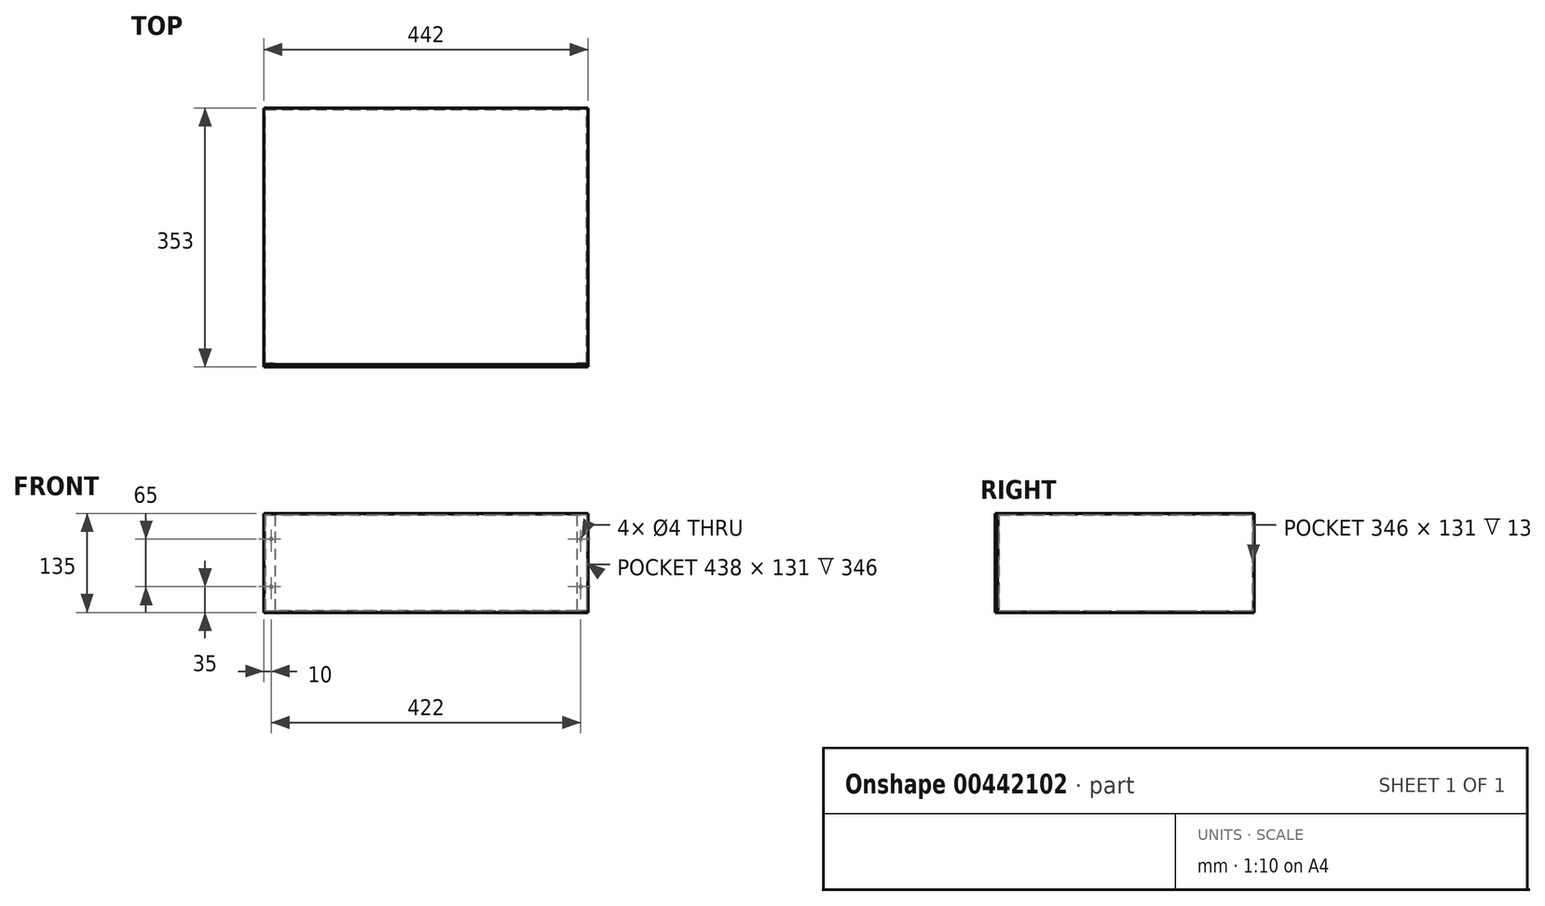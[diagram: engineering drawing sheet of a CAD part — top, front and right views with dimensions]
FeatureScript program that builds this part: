
annotation { "Feature Type Name" : "Feature", "Feature Type Description" : "" }
export const myFeature = defineFeature(function(context is Context, id is Id, definition is map)
    precondition{}
    {
        {
            var Q0;
            Q0=qCreatedBy(makeId("Top.planeOp"),FACE);
            var sketch = newSketch(context, id + "F0", { "sketchPlane" : qUnion([Q0])});
            skLineSegment(sketch, "E0.bottom", {"start": v(221, 175) * mm, "end": v(-221, 175) * mm});
            skLineSegment(sketch, "E0.top", {"start": v(221, -175) * mm, "end": v(-221, -175) * mm});
            skLineSegment(sketch, "E0.left", {"start": v(221, 175) * mm, "end": v(221, -175) * mm});
            skLineSegment(sketch, "E0.right", {"start": v(-221, 175) * mm, "end": v(-221, -175) * mm});
            skPoint(sketch, "E0.middle", {"position": v(0, 0) * mm});
            skSolve(sketch);
        }
        {
            var Q0;
            Q0=qCreatedBy(makeId("Front.planeOp"),FACE);
            cPlane(context, id + "F1", {"entities" : qUnion([Q0]), "cplaneType" : CPlaneType.OFFSET, "offset" : 175 * mm, "width" : 150 * mm, "height" : 150 * mm});
        }
        {
            var Q0;
            Q0=qCreatedBy(makeId("Front.planeOp"),FACE);
            cPlane(context, id + "F2", {"entities" : qUnion([Q0]), "cplaneType" : CPlaneType.OFFSET, "offset" : 175 * mm, "oppositeDirection" : true, "width" : 150 * mm, "height" : 150 * mm});
        }
        {
            var Q0;
            Q0=qCreatedBy(makeId("Top.planeOp"),FACE);
            cPlane(context, id + "F3", {"entities" : qUnion([Q0]), "cplaneType" : CPlaneType.OFFSET, "offset" : 133 * mm, "width" : 150 * mm, "height" : 150 * mm});
        }
        {
            var Q0;
            Q0=qCreatedBy(id+"F3.planeOp",FACE);
            var sketch = newSketch(context, id + "F4", { "sketchPlane" : qUnion([Q0])});
            skLineSegment(sketch, "E1.0", {"start": v(-221, 175) * mm, "end": v(-221, -175) * mm});
            skLineSegment(sketch, "E2.0", {"start": v(221, 175) * mm, "end": v(-221, 175) * mm});
            skLineSegment(sketch, "E3.0", {"start": v(221, 175) * mm, "end": v(221, -175) * mm});
            skLineSegment(sketch, "E4.0", {"start": v(221, -175) * mm, "end": v(-221, -175) * mm});
            skSolve(sketch);
        }
        {
            var Q0;
            Q0=qCreatedBy(makeId("Right.planeOp"),FACE);
            cPlane(context, id + "F5", {"entities" : qUnion([Q0]), "cplaneType" : CPlaneType.OFFSET, "offset" : 221 * mm, "width" : 150 * mm, "height" : 150 * mm});
        }
        {
            var Q0;
            Q0=qCreatedBy(makeId("Right.planeOp"),FACE);
            cPlane(context, id + "F6", {"entities" : qUnion([Q0]), "cplaneType" : CPlaneType.OFFSET, "offset" : 221 * mm, "oppositeDirection" : true, "width" : 150 * mm, "height" : 150 * mm});
        }
        {
            var Q0;
            Q0=makeQuery(id+"F4.imprint","IMPRINT",FACE,{"disambiguationData":[TD([[makeQuery(id+"F4.imprint","IMPRINT",EDGE,{"derivedFrom":sQuery(id+"F4.wireOp",EDGE,"E1.0")}),1.0]])]});
            extrude(context, id + "F7", {"entities" : qUnion([Q0]), "depth" : 2 * mm});
        }
        {
            var Q0;
            Q0=makeQuery(id+"F0.imprint","IMPRINT",FACE,{"disambiguationData":[TD([[makeQuery(id+"F0.imprint","IMPRINT",EDGE,{"derivedFrom":sQuery(id+"F0.wireOp",EDGE,"E0.bottom")}),1.0]])]});
            extrude(context, id + "F8", {"entities" : qUnion([Q0]), "depth" : 2 * mm});
        }
        {
            var Q0;
            Q0=qCreatedBy(id+"F2.planeOp",FACE);
            var sketch = newSketch(context, id + "F9", { "sketchPlane" : qUnion([Q0])});
            skLineSegment(sketch, "E5.bottom", {"start": v(-221, 2) * mm, "end": v(221, 2) * mm});
            skLineSegment(sketch, "E5.top", {"start": v(-221, 133) * mm, "end": v(221, 133) * mm});
            skLineSegment(sketch, "E5.left", {"start": v(-221, 2) * mm, "end": v(-221, 133) * mm});
            skLineSegment(sketch, "E5.right", {"start": v(221, 2) * mm, "end": v(221, 133) * mm});
            skSolve(sketch);
        }
        {
            var Q0;
            Q0=makeQuery(id+"F9.imprint","IMPRINT",FACE,{"disambiguationData":[TD([[makeQuery(id+"F9.imprint","IMPRINT",EDGE,{"derivedFrom":sQuery(id+"F9.wireOp",EDGE,"E5.bottom")}),1.0]])]});
            extrude(context, id + "F10", {"entities" : qUnion([Q0]), "depth" : 2 * mm});
        }
        {
            var Q0;
            Q0=qCreatedBy(id+"F6.planeOp",FACE);
            var sketch = newSketch(context, id + "F11", { "sketchPlane" : qUnion([Q0])});
            skLineSegment(sketch, "E6.bottom", {"start": v(-175, 2) * mm, "end": v(173, 2) * mm});
            skLineSegment(sketch, "E6.top", {"start": v(-175, 133) * mm, "end": v(173, 133) * mm});
            skLineSegment(sketch, "E6.left", {"start": v(-175, 2) * mm, "end": v(-175, 133) * mm});
            skLineSegment(sketch, "E6.right", {"start": v(173, 2) * mm, "end": v(173, 133) * mm});
            skSolve(sketch);
        }
        {
            var Q0;
            Q0=makeQuery(id+"F11.imprint","IMPRINT",FACE,{"disambiguationData":[TD([[makeQuery(id+"F11.imprint","IMPRINT",EDGE,{"derivedFrom":sQuery(id+"F11.wireOp",EDGE,"E6.bottom")}),1.0]])]});
            extrude(context, id + "F12", {"entities" : qUnion([Q0]), "operationType" : NewBodyOperationType.ADD, "depth" : 2 * mm});
        }
        {
            var Q0;
            Q0=qCreatedBy(id+"F5.planeOp",FACE);
            var sketch = newSketch(context, id + "F13", { "sketchPlane" : qUnion([Q0])});
            skLineSegment(sketch, "E7.bottom", {"start": v(-175, 2) * mm, "end": v(173, 2) * mm});
            skLineSegment(sketch, "E7.top", {"start": v(-175, 133) * mm, "end": v(173, 133) * mm});
            skLineSegment(sketch, "E7.left", {"start": v(-175, 2) * mm, "end": v(-175, 133) * mm});
            skLineSegment(sketch, "E7.right", {"start": v(173, 2) * mm, "end": v(173, 133) * mm});
            skSolve(sketch);
        }
        {
            var Q0;
            Q0=makeQuery(id+"F13.imprint","IMPRINT",FACE,{"disambiguationData":[TD([[makeQuery(id+"F13.imprint","IMPRINT",EDGE,{"derivedFrom":sQuery(id+"F13.wireOp",EDGE,"E7.bottom")}),1.0]])]});
            extrude(context, id + "F14", {"entities" : qUnion([Q0]), "operationType" : NewBodyOperationType.ADD, "oppositeDirection" : true, "depth" : 2 * mm});
        }
        {
            var Q0;
            Q0=qCreatedBy(id+"F1.planeOp",FACE);
            var sketch = newSketch(context, id + "F15", { "sketchPlane" : qUnion([Q0])});
            skLineSegment(sketch, "E8.bottom", {"start": v(-219, 133) * mm, "end": v(-206, 133) * mm});
            skLineSegment(sketch, "E8.top", {"start": v(-219, 2) * mm, "end": v(-206, 2) * mm});
            skLineSegment(sketch, "E8.left", {"start": v(-219, 133) * mm, "end": v(-219, 2) * mm});
            skLineSegment(sketch, "E8.right", {"start": v(-206, 133) * mm, "end": v(-206, 2) * mm});
            skLineSegment(sketch, "E9.bottom", {"start": v(219, 133) * mm, "end": v(206, 133) * mm});
            skLineSegment(sketch, "E9.top", {"start": v(219, 2) * mm, "end": v(206, 2) * mm});
            skLineSegment(sketch, "E9.left", {"start": v(219, 133) * mm, "end": v(219, 2) * mm});
            skLineSegment(sketch, "E9.right", {"start": v(206, 133) * mm, "end": v(206, 2) * mm});
            skCircle(sketch, "E10", {"center": v(-211, 100) * mm, "radius": 2 * mm});
            skCircle(sketch, "E11", {"center": v(-211, 35) * mm, "radius": 2 * mm});
            skCircle(sketch, "E12", {"center": v(211, 100) * mm, "radius": 2 * mm});
            skCircle(sketch, "E13", {"center": v(211, 35) * mm, "radius": 2 * mm});
            skSolve(sketch);
        }
        {
            var Q0;
            Q0 = qSketchRegion(id + "F15", true);
            extrude(context, id + "F16", {"entities" : qUnion([Q0]), "operationType" : NewBodyOperationType.ADD, "oppositeDirection" : true, "depth" : 2 * mm});
        }
        {
            var Q0;
            Q0=qCreatedBy(id+"F1.planeOp",FACE);
            var sketch = newSketch(context, id + "F17", { "sketchPlane" : qUnion([Q0])});
            skLineSegment(sketch, "E14.bottom", {"start": v(-221, 135) * mm, "end": v(221, 135) * mm});
            skLineSegment(sketch, "E14.top", {"start": v(-221, 0) * mm, "end": v(221, 0) * mm});
            skLineSegment(sketch, "E14.left", {"start": v(-221, 0) * mm, "end": v(-221, 135) * mm});
            skLineSegment(sketch, "E14.right", {"start": v(221, 0) * mm, "end": v(221, 135) * mm});
            skCircle(sketch, "E15.0", {"center": v(-211, 100) * mm, "radius": 2 * mm, "construction": true});
            skCircle(sketch, "E16.0", {"center": v(-211, 35) * mm, "radius": 2 * mm, "construction": true});
            skCircle(sketch, "E17.0", {"center": v(211, 35) * mm, "radius": 2 * mm, "construction": true});
            skCircle(sketch, "E18.0", {"center": v(211, 100) * mm, "radius": 2 * mm, "construction": true});
            skLineSegment(sketch, "E19.0.0", {"start": v(-221, 133) * mm, "end": v(-221, 2) * mm, "construction": true});
            skLineSegment(sketch, "E19.0.1", {"start": v(-221, 2) * mm, "end": v(-206, 2) * mm, "construction": true});
            skLineSegment(sketch, "E19.0.2", {"start": v(-206, 2) * mm, "end": v(-206, 133) * mm, "construction": true});
            skLineSegment(sketch, "E19.0.3", {"start": v(-206, 133) * mm, "end": v(-221, 133) * mm, "construction": true});
            skLineSegment(sketch, "E20.0.0", {"start": v(221, 2) * mm, "end": v(221, 133) * mm, "construction": true});
            skLineSegment(sketch, "E20.0.1", {"start": v(221, 133) * mm, "end": v(206, 133) * mm, "construction": true});
            skLineSegment(sketch, "E20.0.2", {"start": v(206, 133) * mm, "end": v(206, 2) * mm, "construction": true});
            skLineSegment(sketch, "E20.0.3", {"start": v(206, 2) * mm, "end": v(221, 2) * mm, "construction": true});
            skSolve(sketch);
        }
        {
            var Q0;
            Q0 = qSketchRegion(id + "F17", true);
            extrude(context, id + "F18", {"entities" : qUnion([Q0]), "depth" : 3 * mm});
        }
    });
